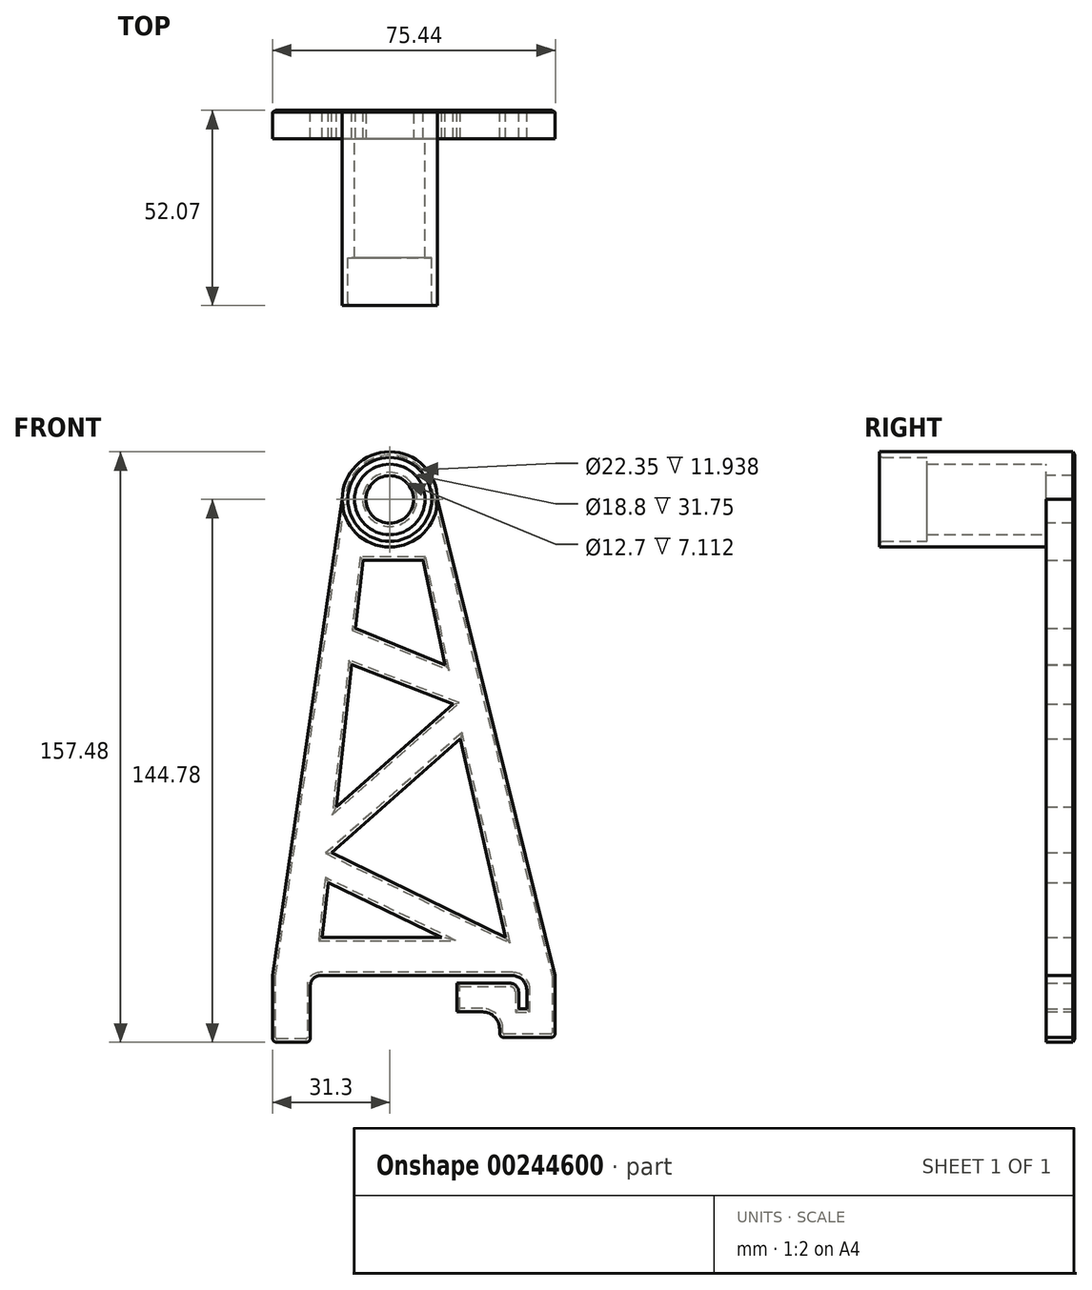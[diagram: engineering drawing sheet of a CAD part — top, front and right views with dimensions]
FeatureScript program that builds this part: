
annotation { "Feature Type Name" : "Feature", "Feature Type Description" : "" }
export const myFeature = defineFeature(function(context is Context, id is Id, definition is map)
    precondition{}
    {
        {
            var Q0;
            Q0=qCreatedBy(makeId("Front.planeOp"),FACE);
            var sketch = newSketch(context, id + "F0", { "sketchPlane" : qUnion([Q0])});
            skLineSegment(sketch, "E0", {"start": v(-18.6, 0) * mm, "end": v(32.7, 0) * mm});
            skLineSegment(sketch, "E1", {"start": v(36.52, -3.8) * mm, "end": v(36.52, -8.9) * mm});
            skLineSegment(sketch, "E2", {"start": v(36.52, -8.9) * mm, "end": v(34.36, -8.9) * mm});
            skLineSegment(sketch, "E3", {"start": v(30.55, -16.51) * mm, "end": v(42.87, -16.51) * mm});
            skLineSegment(sketch, "E4", {"start": v(44.14, -15.24) * mm, "end": v(44.14, 0) * mm});
            skLineSegment(sketch, "E5", {"start": v(44.14, 0) * mm, "end": v(12.7, 127) * mm});
            skLineSegment(sketch, "E6", {"start": v(-12.7, 127) * mm, "end": v(-31.3, 0) * mm});
            skLineSegment(sketch, "E7", {"start": v(-31.3, 0) * mm, "end": v(-31.3, -16.51) * mm});
            skLineSegment(sketch, "E8", {"start": v(-30.03, -17.78) * mm, "end": v(-22.41, -17.78) * mm});
            skLineSegment(sketch, "E9", {"start": v(-21.14, -16.51) * mm, "end": v(-21.14, -2.54) * mm});
            skArc(sketch, "E10", {"start": v(12.7, 127) * mm, "mid": v(0, 139.7) * mm, "end": v(-12.7, 127) * mm});
            skLineSegment(sketch, "E11", {"start": v(-17.5, 10.26) * mm, "end": v(13.86, 10.26) * mm});
            skLineSegment(sketch, "E12", {"start": v(8.87, 110.85) * mm, "end": v(-7.14, 110.85) * mm});
            skLineSegment(sketch, "E13", {"start": v(-7.14, 110.85) * mm, "end": v(-9.1, 92.68) * mm});
            skLineSegment(sketch, "E14", {"start": v(-17.99, 10.26) * mm, "end": v(-17.5, 10.26) * mm});
            skLineSegment(sketch, "E15", {"start": v(-15.55, 32.85) * mm, "end": v(18.8, 63.2) * mm});
            skLineSegment(sketch, "E16", {"start": v(-14.24, 45.02) * mm, "end": v(16.87, 72.47) * mm});
            skLineSegment(sketch, "E17", {"start": v(16.87, 72.47) * mm, "end": v(-10.15, 82.94) * mm});
            skLineSegment(sketch, "E18", {"start": v(-9.1, 92.68) * mm, "end": v(14.7, 82.88) * mm});
            skLineSegment(sketch, "E19", {"start": v(-15.55, 32.85) * mm, "end": v(30.9, 10.26) * mm});
            skLineSegment(sketch, "E20", {"start": v(-16.41, 24.87) * mm, "end": v(13.86, 10.26) * mm});
            skLineSegment(sketch, "E21.trimOffspring", {"start": v(-16.41, 24.87) * mm, "end": v(-17.99, 10.26) * mm});
            skLineSegment(sketch, "E22.trimOffspring", {"start": v(14.7, 82.88) * mm, "end": v(8.87, 110.85) * mm});
            skLineSegment(sketch, "E23.trimOffspring", {"start": v(-10.15, 82.94) * mm, "end": v(-14.24, 45.02) * mm});
            skLineSegment(sketch, "E24", {"start": v(18.8, 63.2) * mm, "end": v(30.9, 10.26) * mm});
            skLineSegment(sketch, "E25", {"start": v(29.28, -15.24) * mm, "end": v(29.28, -14.22) * mm});
            skLineSegment(sketch, "E26", {"start": v(29.28, -2.03) * mm, "end": v(32.07, -2.03) * mm});
            skLineSegment(sketch, "E27", {"start": v(34.36, -4.32) * mm, "end": v(34.36, -8.9) * mm});
            skPoint(sketch, "E28.visualSharp", {"position": v(36.52, 0) * mm});
            skArc(sketch, "E28.filletArc", {"start": v(36.52, -3.8) * mm, "mid": v(35.4, -1.12) * mm, "end": v(32.7, 0) * mm});
            skPoint(sketch, "E29.visualSharp", {"position": v(-21.14, 0) * mm});
            skArc(sketch, "E29.filletArc", {"start": v(-18.6, 0) * mm, "mid": v(-20.4, -0.74) * mm, "end": v(-21.14, -2.54) * mm});
            skLineSegment(sketch, "E30", {"start": v(29.28, -2.03) * mm, "end": v(17.85, -2.03) * mm});
            skLineSegment(sketch, "E31", {"start": v(17.85, -2.03) * mm, "end": v(17.85, -9.65) * mm});
            skLineSegment(sketch, "E32", {"start": v(17.85, -9.65) * mm, "end": v(24.7, -9.65) * mm});
            skPoint(sketch, "E33.visualSharp", {"position": v(34.36, -2.03) * mm});
            skArc(sketch, "E33.filletArc", {"start": v(34.36, -4.32) * mm, "mid": v(33.69, -2.7) * mm, "end": v(32.07, -2.03) * mm});
            skPoint(sketch, "E34.visualSharp", {"position": v(29.28, -9.65) * mm});
            skArc(sketch, "E34.filletArc", {"start": v(29.28, -14.22) * mm, "mid": v(27.94, -11) * mm, "end": v(24.7, -9.65) * mm});
            skPoint(sketch, "E35.visualSharp", {"position": v(29.28, -16.51) * mm});
            skArc(sketch, "E35.filletArc", {"start": v(29.28, -15.24) * mm, "mid": v(29.65, -16.14) * mm, "end": v(30.55, -16.51) * mm});
            skPoint(sketch, "E36.visualSharp", {"position": v(44.14, -16.5) * mm});
            skArc(sketch, "E36.filletArc", {"start": v(42.87, -16.5) * mm, "mid": v(43.76, -16.14) * mm, "end": v(44.14, -15.24) * mm});
            skPoint(sketch, "E37.visualSharp", {"position": v(-21.14, -17.78) * mm});
            skArc(sketch, "E37.filletArc", {"start": v(-22.41, -17.78) * mm, "mid": v(-21.51, -17.4) * mm, "end": v(-21.14, -16.51) * mm});
            skPoint(sketch, "E38.visualSharp", {"position": v(-31.3, -17.78) * mm});
            skArc(sketch, "E38.filletArc", {"start": v(-31.3, -16.51) * mm, "mid": v(-30.93, -17.4) * mm, "end": v(-30.03, -17.78) * mm});
            skSolve(sketch);
        }
        {
            var Q0;
            Q0=qSketchRegion(id+"F0",true);
            extrude(context, id + "F1", {"entities" : qUnion([Q0]), "depth" : 7.62 * mm});
        }
        {
            var Q0;
            Q0=makeQuery(id+"F1.opExtrude","CAP_FACE",FACE,{"disambiguationData":[OSD([sQuery(id+"F0.wireOp",EDGE,"E0"),sQuery(id+"F0.wireOp",EDGE,"E1"),sQuery(id+"F0.wireOp",EDGE,"E2"),sQuery(id+"F0.wireOp",EDGE,"E3"),sQuery(id+"F0.wireOp",EDGE,"E4"),sQuery(id+"F0.wireOp",EDGE,"E5"),sQuery(id+"F0.wireOp",EDGE,"E6"),sQuery(id+"F0.wireOp",EDGE,"E7"),sQuery(id+"F0.wireOp",EDGE,"E8"),sQuery(id+"F0.wireOp",EDGE,"E9"),sQuery(id+"F0.wireOp",EDGE,"85a4300b-4fb4-4320-8566-280c9bc53024"),sQuery(id+"F0.wireOp",EDGE,"pHLkkCRf-vtNH-Kyco-QB3F-mwyPBLed3uRI"),sQuery(id+"F0.wireOp",EDGE,"E10"),sQuery(id+"F0.wireOp",EDGE,"E11"),sQuery(id+"F0.wireOp",EDGE,"E12"),sQuery(id+"F0.wireOp",EDGE,"E13"),sQuery(id+"F0.wireOp",EDGE,"E14"),sQuery(id+"F0.wireOp",EDGE,"E15"),sQuery(id+"F0.wireOp",EDGE,"E16"),sQuery(id+"F0.wireOp",EDGE,"E17"),sQuery(id+"F0.wireOp",EDGE,"E18"),sQuery(id+"F0.wireOp",EDGE,"E19"),sQuery(id+"F0.wireOp",EDGE,"E20"),sQuery(id+"F0.wireOp",EDGE,"E21.trimOffspring"),sQuery(id+"F0.wireOp",EDGE,"E22.trimOffspring"),sQuery(id+"F0.wireOp",EDGE,"E23.trimOffspring"),sQuery(id+"F0.wireOp",EDGE,"E24")])],"isStart":false});
            var sketch = newSketch(context, id + "F2", { "sketchPlane" : qUnion([Q0])});
            skCircle(sketch, "E39", {"center": v(0, 127) * mm, "radius": 12.7 * mm});
            skCircle(sketch, "E40", {"center": v(0, 127) * mm, "radius": 9.4 * mm});
            skSolve(sketch);
        }
        {
            var Q0;
            Q0=qSketchRegion(id+"F2",true);
            extrude(context, id + "F3", {"entities" : qUnion([Q0]), "operationType" : NewBodyOperationType.ADD, "depth" : 31.75 * mm});
        }
        {
            var Q0;
            Q0=makeQuery(id+"F3.opExtrude","CAP_FACE",FACE,{"disambiguationData":[OSD([sQuery(id+"F2.wireOp",EDGE,"E39"),sQuery(id+"F2.wireOp",EDGE,"E40")])],"isStart":false});
            var sketch = newSketch(context, id + "F4", { "sketchPlane" : qUnion([Q0])});
            skCircle(sketch, "E41", {"center": v(0, 127) * mm, "radius": 12.7 * mm});
            skCircle(sketch, "E42", {"center": v(0, 127) * mm, "radius": 11.18 * mm});
            skSolve(sketch);
        }
        {
            var Q0;
            Q0=qSketchRegion(id+"F4",true);
            extrude(context, id + "F5", {"entities" : qUnion([Q0]), "operationType" : NewBodyOperationType.ADD, "depth" : 12.7 * mm});
        }
        {
            var Q0;
            Q0=makeQuery(id+"F3.boolean.opBoolean","SPLIT",FACE,{"disambiguationData":[TD([makeQuery(id+"F3.opExtrude","SWEPT_FACE",FACE,{"disambiguationData":[OSD([sQuery(id+"F2.wireOp",EDGE,"E40")])]})])],"derivedFrom":makeQuery(id+"F1.opExtrude","CAP_FACE",FACE,{"disambiguationData":[OSD([sQuery(id+"F0.wireOp",EDGE,"E0"),sQuery(id+"F0.wireOp",EDGE,"E1"),sQuery(id+"F0.wireOp",EDGE,"E2"),sQuery(id+"F0.wireOp",EDGE,"E3"),sQuery(id+"F0.wireOp",EDGE,"E4"),sQuery(id+"F0.wireOp",EDGE,"E5"),sQuery(id+"F0.wireOp",EDGE,"E6"),sQuery(id+"F0.wireOp",EDGE,"E7"),sQuery(id+"F0.wireOp",EDGE,"E8"),sQuery(id+"F0.wireOp",EDGE,"E9"),sQuery(id+"F0.wireOp",EDGE,"E10"),sQuery(id+"F0.wireOp",EDGE,"E11"),sQuery(id+"F0.wireOp",EDGE,"E12"),sQuery(id+"F0.wireOp",EDGE,"E13"),sQuery(id+"F0.wireOp",EDGE,"E14"),sQuery(id+"F0.wireOp",EDGE,"E15"),sQuery(id+"F0.wireOp",EDGE,"E16"),sQuery(id+"F0.wireOp",EDGE,"E17"),sQuery(id+"F0.wireOp",EDGE,"E18"),sQuery(id+"F0.wireOp",EDGE,"E19"),sQuery(id+"F0.wireOp",EDGE,"E20"),sQuery(id+"F0.wireOp",EDGE,"E21.trimOffspring"),sQuery(id+"F0.wireOp",EDGE,"E22.trimOffspring"),sQuery(id+"F0.wireOp",EDGE,"E23.trimOffspring"),sQuery(id+"F0.wireOp",EDGE,"E24"),sQuery(id+"F0.wireOp",EDGE,"E25"),sQuery(id+"F0.wireOp",EDGE,"E26"),sQuery(id+"F0.wireOp",EDGE,"E27"),sQuery(id+"F0.wireOp",EDGE,"E28.filletArc"),sQuery(id+"F0.wireOp",EDGE,"E29.filletArc"),sQuery(id+"F0.wireOp",EDGE,"E30"),sQuery(id+"F0.wireOp",EDGE,"E31"),sQuery(id+"F0.wireOp",EDGE,"E32"),sQuery(id+"F0.wireOp",EDGE,"E33.filletArc"),sQuery(id+"F0.wireOp",EDGE,"E34.filletArc"),sQuery(id+"F0.wireOp",EDGE,"E35.filletArc"),sQuery(id+"F0.wireOp",EDGE,"E36.filletArc"),sQuery(id+"F0.wireOp",EDGE,"E37.filletArc"),sQuery(id+"F0.wireOp",EDGE,"E38.filletArc")])],"isStart":false})});
            var sketch = newSketch(context, id + "F6", { "sketchPlane" : qUnion([Q0])});
            skCircle(sketch, "E43", {"center": v(0, 127) * mm, "radius": 6.35 * mm});
            skSolve(sketch);
        }
        {
            var Q0;
            Q0 = qSketchRegion(id + "F6", true);
            extrude(context, id + "F7", {"entities" : qUnion([Q0]), "operationType" : NewBodyOperationType.REMOVE, "oppositeDirection" : true, "depth" : 25.4 * mm});
        }
        {
            var Q0;
            Q0=makeQuery(id+"F5.opExtrude","CAP_EDGE",EDGE,{"disambiguationData":[OSD([sQuery(id+"F4.wireOp",EDGE,"E42")])],"isStart":false});
            fillet(context, id + "F8", {"entities" : qUnion([Q0]), "radius" : 0.76 * mm, "tangentPropagation" : true, "allowEdgeOverflow" : false});
        }
        {
            var Q0;
            Q0=makeQuery(id+"F1.opExtrude","CAP_FACE",FACE,{"disambiguationData":[OSD([sQuery(id+"F0.wireOp",EDGE,"E0"),sQuery(id+"F0.wireOp",EDGE,"E1"),sQuery(id+"F0.wireOp",EDGE,"E2"),sQuery(id+"F0.wireOp",EDGE,"E3"),sQuery(id+"F0.wireOp",EDGE,"E4"),sQuery(id+"F0.wireOp",EDGE,"E5"),sQuery(id+"F0.wireOp",EDGE,"E6"),sQuery(id+"F0.wireOp",EDGE,"E7"),sQuery(id+"F0.wireOp",EDGE,"E8"),sQuery(id+"F0.wireOp",EDGE,"E9"),sQuery(id+"F0.wireOp",EDGE,"E10"),sQuery(id+"F0.wireOp",EDGE,"E11"),sQuery(id+"F0.wireOp",EDGE,"E12"),sQuery(id+"F0.wireOp",EDGE,"E13"),sQuery(id+"F0.wireOp",EDGE,"E14"),sQuery(id+"F0.wireOp",EDGE,"E15"),sQuery(id+"F0.wireOp",EDGE,"E16"),sQuery(id+"F0.wireOp",EDGE,"E17"),sQuery(id+"F0.wireOp",EDGE,"E18"),sQuery(id+"F0.wireOp",EDGE,"E19"),sQuery(id+"F0.wireOp",EDGE,"E20"),sQuery(id+"F0.wireOp",EDGE,"E21.trimOffspring"),sQuery(id+"F0.wireOp",EDGE,"E22.trimOffspring"),sQuery(id+"F0.wireOp",EDGE,"E23.trimOffspring"),sQuery(id+"F0.wireOp",EDGE,"E24"),sQuery(id+"F0.wireOp",EDGE,"E25"),sQuery(id+"F0.wireOp",EDGE,"E26"),sQuery(id+"F0.wireOp",EDGE,"E27"),sQuery(id+"F0.wireOp",EDGE,"E28.filletArc"),sQuery(id+"F0.wireOp",EDGE,"E29.filletArc"),sQuery(id+"F0.wireOp",EDGE,"E30"),sQuery(id+"F0.wireOp",EDGE,"E31"),sQuery(id+"F0.wireOp",EDGE,"E32"),sQuery(id+"F0.wireOp",EDGE,"E33.filletArc"),sQuery(id+"F0.wireOp",EDGE,"E34.filletArc"),sQuery(id+"F0.wireOp",EDGE,"E35.filletArc"),sQuery(id+"F0.wireOp",EDGE,"E36.filletArc"),sQuery(id+"F0.wireOp",EDGE,"E37.filletArc"),sQuery(id+"F0.wireOp",EDGE,"E38.filletArc")])],"isStart":true});
            chamfer(context, id + "F9", {"entities" : qUnion([Q0]), "chamferType" : ChamferType.OFFSET_ANGLE, "width" : 0.5 * mm, "oppositeDirection" : false, "angle" : 60 * degree, "tangentPropagation" : true});
        }
    });
